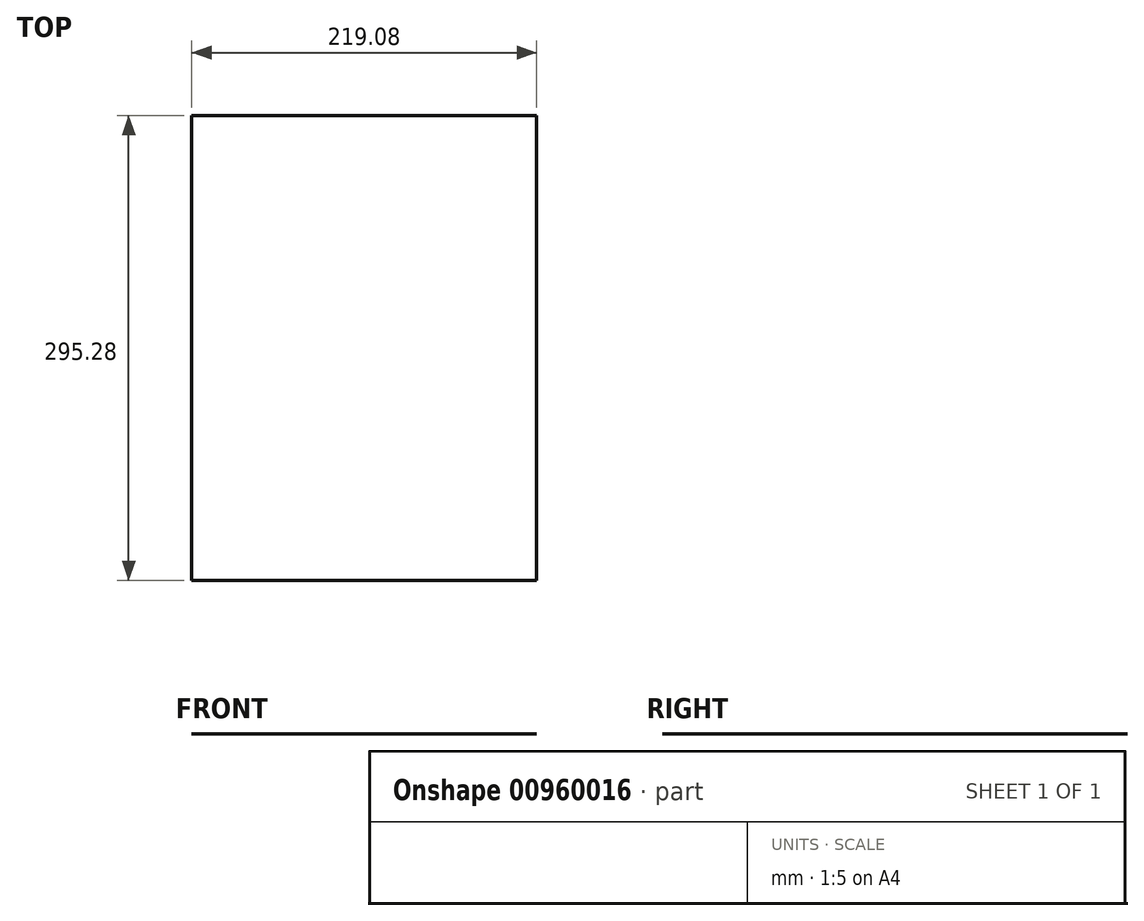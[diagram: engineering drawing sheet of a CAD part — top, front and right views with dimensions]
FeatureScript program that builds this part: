
annotation { "Feature Type Name" : "Feature", "Feature Type Description" : "" }
export const myFeature = defineFeature(function(context is Context, id is Id, definition is map)
    precondition{}
    {
        {
            var Q0;
            Q0=qCreatedBy(makeId("Top.planeOp"),FACE);
            var sketch = newSketch(context, id + "F0", { "sketchPlane" : qUnion([Q0])});
            skLineSegment(sketch, "E0.bottom", {"start": v(-109.54, 147.64) * mm, "end": v(109.54, 147.64) * mm});
            skLineSegment(sketch, "E0.top", {"start": v(-109.54, -147.64) * mm, "end": v(109.54, -147.64) * mm});
            skLineSegment(sketch, "E0.left", {"start": v(-109.54, 147.64) * mm, "end": v(-109.54, -147.64) * mm});
            skLineSegment(sketch, "E0.right", {"start": v(109.54, 147.64) * mm, "end": v(109.54, -147.64) * mm});
            skSolve(sketch);
        }
        {
            var Q0;
            Q0 = qSketchRegion(id + "F0", true);
            extrude(context, id + "F1", {"entities" : qUnion([Q0]), "depth" : 1 / 203.2 * mm, "offsetDistance" : 25.4 * mm});
        }
    });
